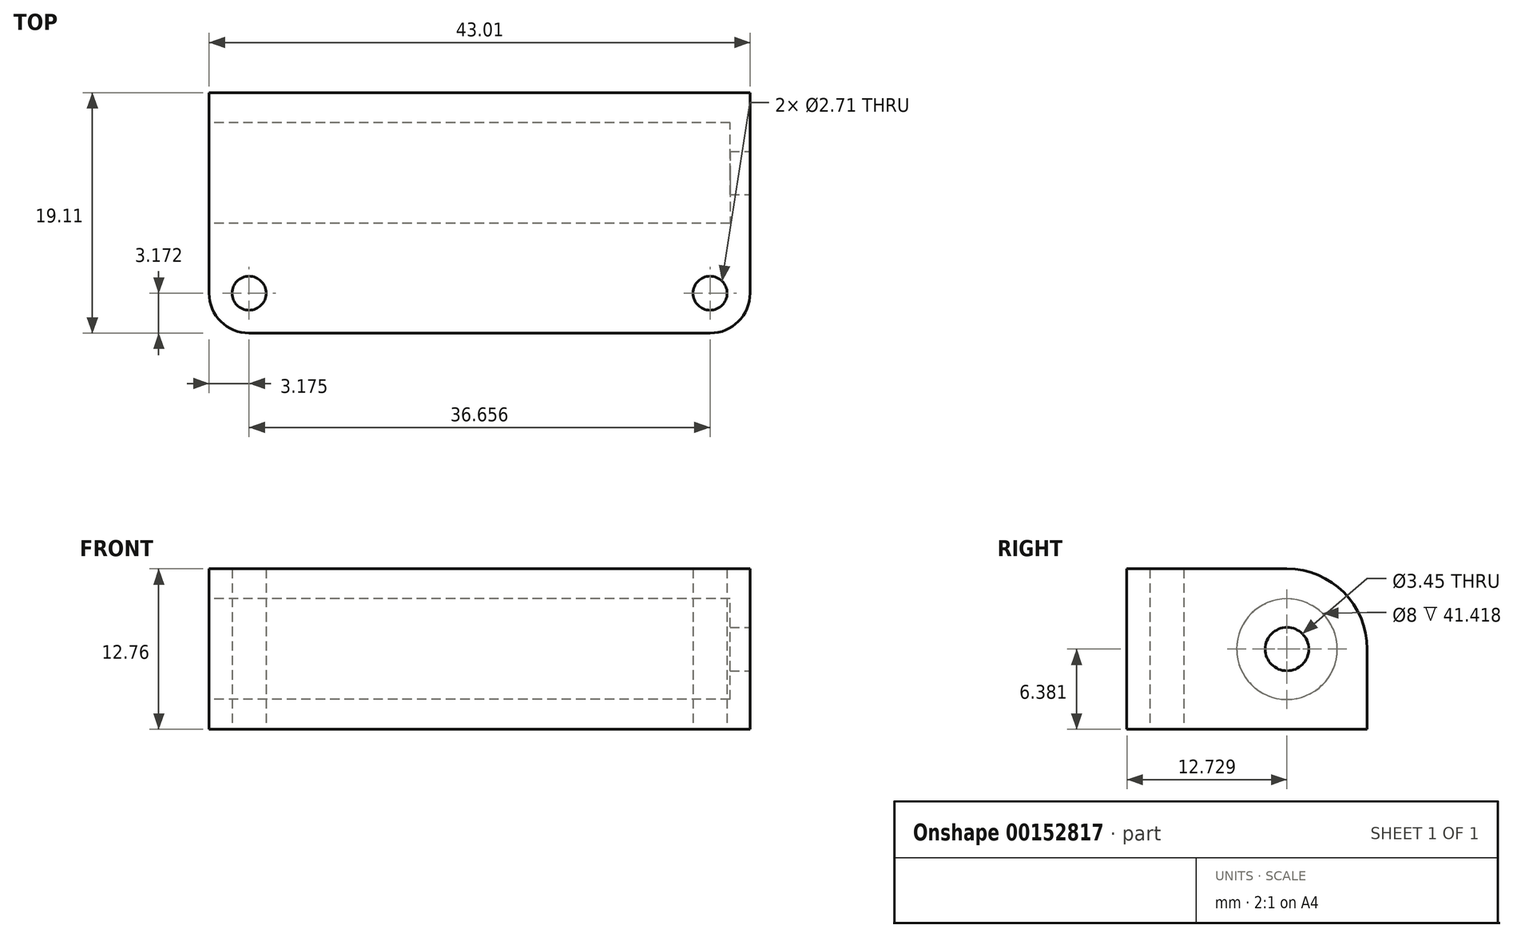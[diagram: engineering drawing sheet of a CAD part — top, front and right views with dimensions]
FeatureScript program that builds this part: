
annotation { "Feature Type Name" : "Feature", "Feature Type Description" : "" }
export const myFeature = defineFeature(function(context is Context, id is Id, definition is map)
    precondition{}
    {
        {
            var Q0;
            Q0=qCreatedBy(makeId("Top.planeOp"),FACE);
            var sketch = newSketch(context, id + "F0", { "sketchPlane" : qUnion([Q0])});
            skLineSegment(sketch, "E0.bottom", {"start": v(0, 0) * mm, "end": v(43, 0) * mm});
            skLineSegment(sketch, "E0.top", {"start": v(0, -19.11) * mm, "end": v(43, -19.11) * mm});
            skLineSegment(sketch, "E0.left", {"start": v(0, -19.11) * mm, "end": v(0, 0) * mm});
            skLineSegment(sketch, "E0.right", {"start": v(43, -19.11) * mm, "end": v(43, 0) * mm});
            skLineSegment(sketch, "E1", {"start": v(0, -15.94) * mm, "end": v(3.18, -15.94) * mm, "construction": true});
            skCircle(sketch, "E2", {"center": v(3.18, -15.94) * mm, "radius": 1.35 * mm});
            skLineSegment(sketch, "E3", {"start": v(43, -15.94) * mm, "end": v(39.83, -15.94) * mm, "construction": true});
            skCircle(sketch, "E4", {"center": v(39.83, -15.94) * mm, "radius": 1.35 * mm});
            skLineSegment(sketch, "E5", {"start": v(3.18, -15.94) * mm, "end": v(3.18, -19.11) * mm, "construction": true});
            skSolve(sketch);
        }
        {
            var Q0;
            Q0=qSketchRegion(id+"F0",true);
            extrude(context, id + "F1", {"entities" : qUnion([Q0]), "depth" : 12.76 * mm});
        }
        {
            var Q0;
            Q0=makeQuery(id+"F1.opExtrude","SWEPT_EDGE",EDGE,{"disambiguationData":[OSD([sQuery(id+"F0.wireOp",EDGE,"E0.top"),sQuery(id+"F0.wireOp",EDGE,"E0.right")])]});
            var Q1;
            Q1=makeQuery(id+"F1.opExtrude","SWEPT_EDGE",EDGE,{"disambiguationData":[OSD([sQuery(id+"F0.wireOp",EDGE,"E0.top"),sQuery(id+"F0.wireOp",EDGE,"E0.left")])]});
            fillet(context, id + "F2", {"entities" : qUnion([Q0, Q1]), "radius" : 3.17 * mm, "allowEdgeOverflow" : false});
        }
        {
            var Q0;
            Q0=makeQuery(id+"F1.opExtrude","CAP_EDGE",EDGE,{"disambiguationData":[OSD([sQuery(id+"F0.wireOp",EDGE,"E0.bottom")])],"isStart":false});
            fillet(context, id + "F3", {"entities" : qUnion([Q0]), "radius" : 6.38 * mm, "tangentPropagation" : true, "allowEdgeOverflow" : false});
        }
        {
            var Q0;
            Q0=makeQuery(id+"F1.opExtrude","SWEPT_FACE",FACE,{"disambiguationData":[OSD([sQuery(id+"F0.wireOp",EDGE,"E0.right")])]});
            var sketch = newSketch(context, id + "F4", { "sketchPlane" : qUnion([Q0])});
            skCircle(sketch, "E6", {"center": v(-6.38, 6.38) * mm, "radius": 1.73 * mm});
            skSolve(sketch);
        }
        {
            var Q0;
            Q0=qSketchRegion(id+"F4",true);
            var Q1;
            Q1=makeQuery(id+"F1.opExtrude","SWEPT_FACE",FACE,{"disambiguationData":[OSD([sQuery(id+"F0.wireOp",EDGE,"E0.left")])]});
            extrude(context, id + "F5", {"entities" : qUnion([Q0]), "operationType" : NewBodyOperationType.REMOVE, "endBound" : BoundingType.UP_TO_SURFACE, "oppositeDirection" : true, "endBoundEntityFace" : qUnion([Q1]), "depth" : 25.4 * mm});
        }
        {
            var Q0;
            Q0=makeQuery(id+"F1.opExtrude","SWEPT_FACE",FACE,{"disambiguationData":[OSD([sQuery(id+"F0.wireOp",EDGE,"E0.left")])]});
            var sketch = newSketch(context, id + "F6", { "sketchPlane" : qUnion([Q0])});
            skCircle(sketch, "E7", {"center": v(6.38, 6.38) * mm, "radius": 4 * mm});
            skSolve(sketch);
        }
        {
            var Q0;
            Q0=makeQuery(id+"F1.opExtrude","SWEPT_FACE",FACE,{"disambiguationData":[OSD([sQuery(id+"F0.wireOp",EDGE,"E0.right")])]});
            cPlane(context, id + "F7", {"entities" : qUnion([Q0]), "cplaneType" : CPlaneType.OFFSET, "offset" : 1.59 * mm, "oppositeDirection" : true, "width" : 152.4 * mm, "height" : 152.4 * mm});
        }
        {
            var Q0;
            Q0=makeQuery(id+"F6.imprint","IMPRINT",FACE,{"disambiguationData":[TD([[makeQuery(id+"F6.imprint","IMPRINT",EDGE,{"derivedFrom":sQuery(id+"F6.wireOp",EDGE,"E7")}),1.0]])]});
            var Q1;
            Q1=qCreatedBy(id+"F7.planeOp",FACE);
            extrude(context, id + "F8", {"entities" : qUnion([Q0]), "operationType" : NewBodyOperationType.REMOVE, "endBound" : BoundingType.UP_TO_SURFACE, "oppositeDirection" : true, "endBoundEntityFace" : qUnion([Q1]), "depth" : 25.4 * mm});
        }
    });
